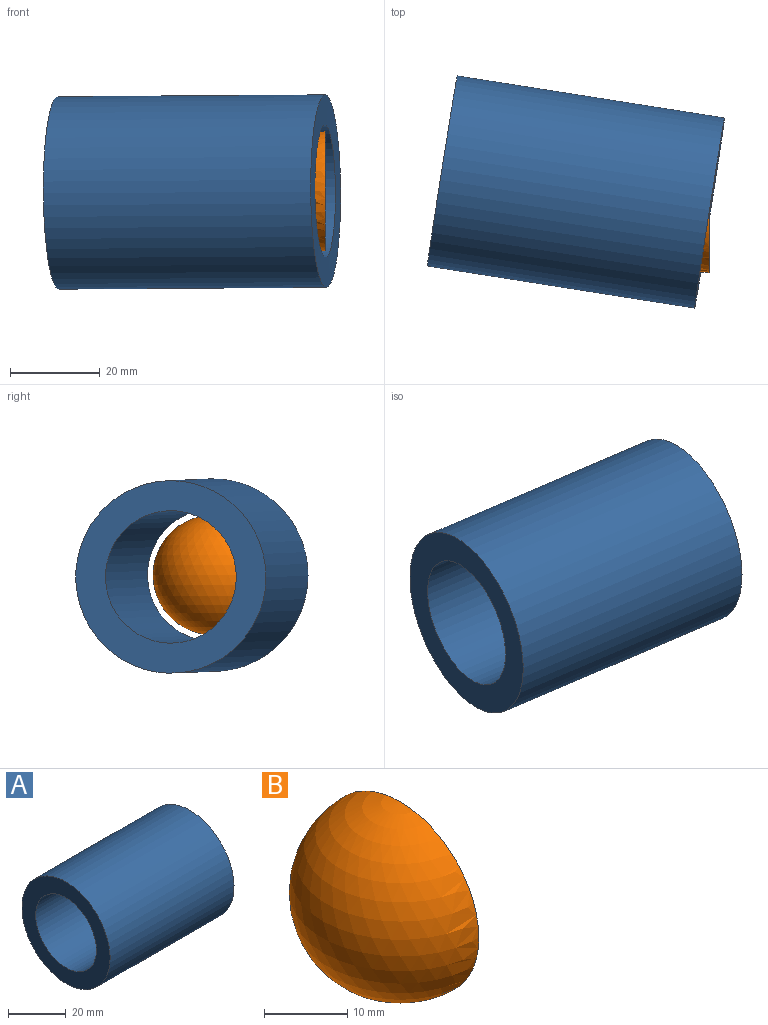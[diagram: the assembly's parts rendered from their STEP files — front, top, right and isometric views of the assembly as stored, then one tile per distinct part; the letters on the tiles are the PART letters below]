
ASSEMBLY  parts=2 mates=1
PART A: 4 faces, bbox 60.4x43x43 mm
  f0: cone r=21.5mm half-angle=89.1deg, axis (1,0,0), area 764.3mm2, adj f1,f3
  f1: cylinder r=21.5mm len=60.44mm, axis (1,0,0), area 8162.8mm2, adj f0,f2
  f2: plane 42.99x42.99mm, normal (-1,0,0), area 764.2mm2, adj f1,f3
  f3: cylinder r=14.79mm len=60.33mm, axis (1,0,0), area 5607.4mm2, adj f0,f2
PART B: 2 faces, bbox 13.3x26.7x26.7 mm
  f0: sphere r=13.34mm, area 1118.2mm2, adj f1
  f1: plane 26.68x26.68mm, normal (1,0,0), area 559.1mm2, adj f0
PLACE A rot(axis=(0.22,-0.06,-0.97),9.2deg) t=(22.67,-3.57,0.16)mm
PLACE B at identity fixed
MATE ball B.f1 <-> A.f0  axis (1,0,0) through (0,0,0)mm
